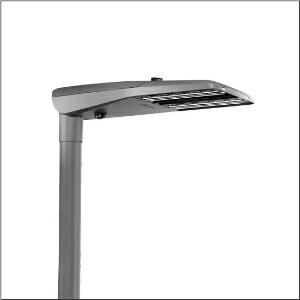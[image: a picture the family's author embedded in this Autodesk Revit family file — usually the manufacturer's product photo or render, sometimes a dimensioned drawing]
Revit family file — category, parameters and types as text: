
# Revit family: streetlight_sl_11_iq_midi___st1_2a_5xc3a51y08le_7352
name_source: partatom
category: Lighting Fixtures
units: mm (PartAtom-declared; Revit-internal decimal feet)

## family parameters
Cut with Voids When Loaded = No
Host = Face
Light Source = No
Part Type = Normal
Room Calculation Point = No
Round Connector Dimension = Use Diameter
Shared = No

## types (1)
- --- (1 x LED, 9210 lm, 59.4 W, 3000K)
    Apparent Load = 59 VA
    CIE Flux Codes = 32 70 96 100 100
    Color Rendering = 70
    Color Temperature = 3000K
    Default Elevation = 1800 mm
    Description = Streetlight SL 11 iQ midi, mast luminaire, primary light control with 3 zone facetted reflector, of plastic, silver coated, highly specular, primary optical cover: cover, of PMMA, transparent, light distribution: ST1.2a, light emission: direct distribution, primary light characteristic: asymmetric, installation type: post-top, side-entry, LED, High Power LED, rated luminous flux: 9.210lm, luminous efficacy: 155lm/W, light colour: 730, colour temperature: 3000K, control: presetting dimming logarithmic, Street-Remote, Auto-Match, Temp-Guard, Lumen-Switch, Night-Set, Smart-Wire, Light-Fading, Desk-Remote (wireless, voltage-free reading and setting of iQ features in the workshop via application-optimized NFC function/RFID function), optimised constant luminous flux control (CLO 2.0), with cable H07RN-F 5x 1.5mm², mains connection: 230..240V, AC, 50/60Hz, connection cable pre-assembled, cable length: 8,5m, start of lifetime: 59W, end of service life: 62W, reduction: 29W, luminaire housing, of diecast aluminium, powder-coated, Siteco® metallic grey (DB 702S), please order mast flange separately, inclination adjustable without tools: 0°, 5°, 10°, 15° (post-top) | 0°, -5°, -10°, -15° (side-entry), sealing non-destructively replaceable, multi-level sealing system, length: 780mm, width: 376mm, height: 118mm, mast flange for spigot size: 42mm (side-entry): 5XC10008XM4, 60/48mm (side-entry/post-top): 5XC10108XM2, 76/60mm (side-entry/post-top): 5XC10108XM1, equipment: standard, Smart Interface below and above, protection rating (complete): IP66, insulation class (complete): insulation class II (safety insulation), certification: CE, ENEC, VDE, UKCA, impact resistance: IK09, permissible operating ambient temperature for outdoor applications: -25..+50°C, standard-compliant lighting for roads and squares, Environmental Product Declaration (EPD) tested and certified by an independent institute, packaging unit: 1 piece

Light Distribution: ST1.2a
    Height = 118 mm
    Lamp = 1 x LED
    Lamp Light Flux = 9210 lm
    Lamp Power = 59.4 W
    Lamp count = 1
    Length = 780 mm
    Luminous efficacy = 155 lm/W
    Manufacturer = Siteco
    ModVariant = No
    Model = 5XC3A51Y08LE
    Number of Poles = 1
    OnlyDefault = Yes
    Power Factor = 1
    Product Name = Streetlight SL 11 iQ midi | ST1.2a
    Product group = mast luminaire | pylon top
    ProductGroupID = 6100
    Protection Class = Protection class II
    Protection Degree = IP 66
    RLX_Detail_Level = 1
    RLX_Emergency_Light_Flux = 0 lm
    RLX_Emergency_Type = 0
    RLX_Emergency_Type_DB = No
    RlxData = <blob elided: 69653 chars, md5=4128ec2e>
    Socket = socket
    Standby Power = 0 W
    System Light Flux = 9210 lm
    System Power = 59 W
    Type Comments = factory setting: luminous flux: 100 % | dim-lin: 254 | 521 mA
    Type Image = l_1004429.jpg
    URL = http://relux.com
    VarID = @adj_064637
    Voltage = 0 V
    Weight = 0.00 kg
    Width = 376 mm

## geometry (parser evidence)
native form markers: Blend x4, Sweep x11
no freeform markers — native parametric forms only
